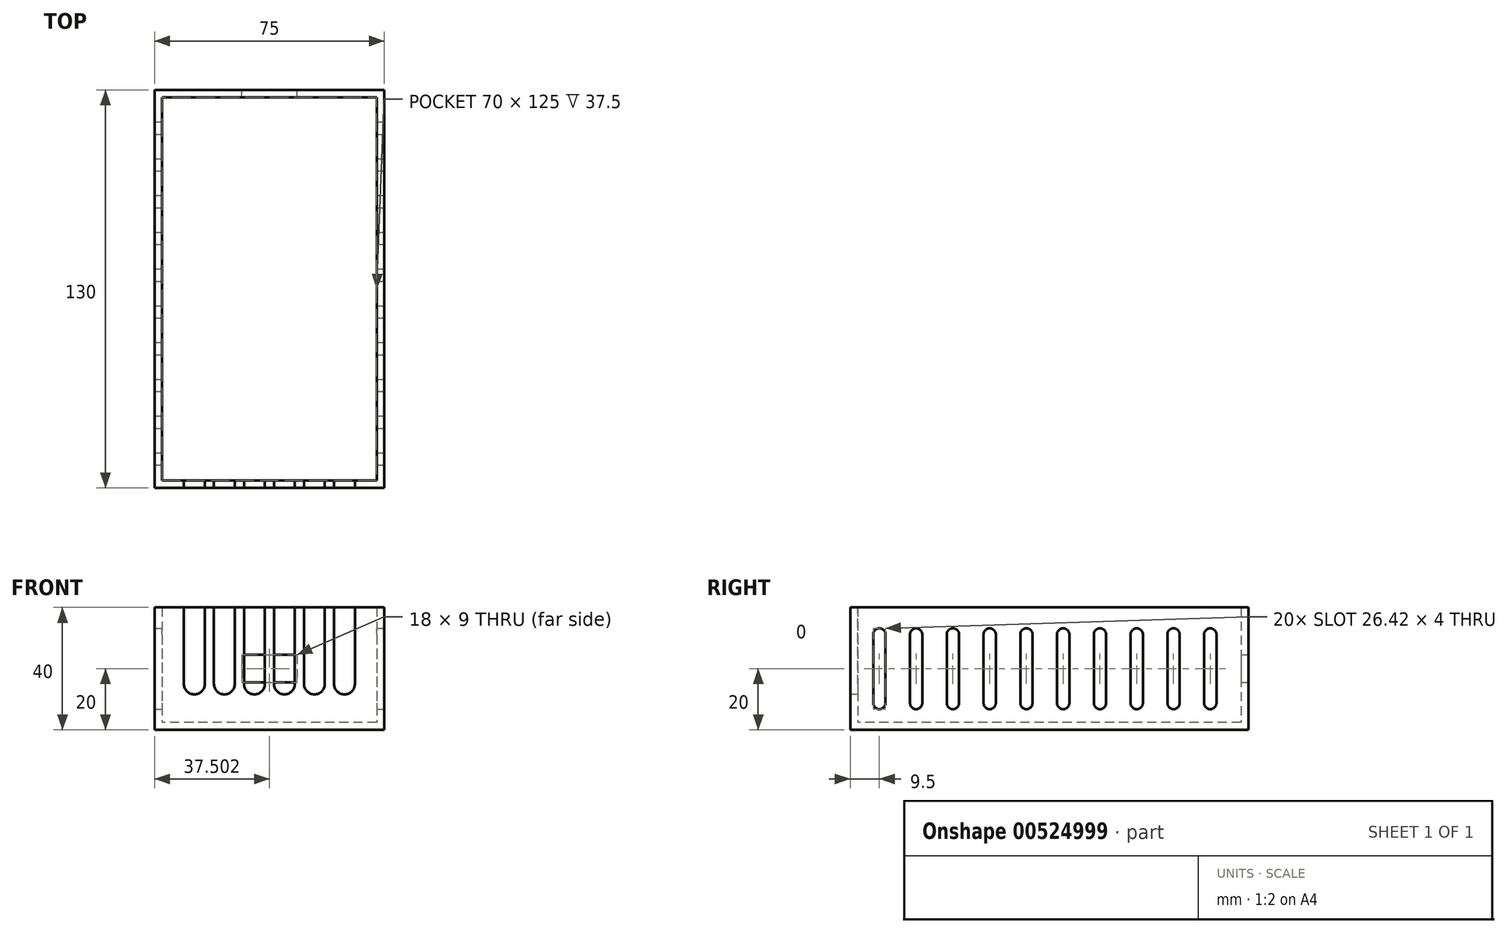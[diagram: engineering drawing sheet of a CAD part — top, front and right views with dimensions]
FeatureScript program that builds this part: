
annotation { "Feature Type Name" : "Feature", "Feature Type Description" : "" }
export const myFeature = defineFeature(function(context is Context, id is Id, definition is map)
    precondition{}
    {
        {
            var Q0;
            Q0=qCreatedBy(makeId("Top.planeOp"),FACE);
            var sketch = newSketch(context, id + "F0", { "sketchPlane" : qUnion([Q0])});
            skLineSegment(sketch, "E0.bottom", {"start": v(40.58, 65) * mm, "end": v(-34.42, 65) * mm});
            skLineSegment(sketch, "E0.top", {"start": v(40.58, -65) * mm, "end": v(-34.42, -65) * mm});
            skLineSegment(sketch, "E0.left", {"start": v(40.58, 65) * mm, "end": v(40.58, -65) * mm});
            skLineSegment(sketch, "E0.right", {"start": v(-34.42, 65) * mm, "end": v(-34.42, -65) * mm});
            skPoint(sketch, "E0.middle", {"position": v(3.08, 0) * mm});
            skSolve(sketch);
        }
        {
            var Q0;
            Q0=makeQuery(id+"F0.imprint","IMPRINT",FACE,{"disambiguationData":[TD([[makeQuery(id+"F0.imprint","IMPRINT",EDGE,{"derivedFrom":sQuery(id+"F0.wireOp",EDGE,"E0.bottom")}),1.0]])]});
            extrude(context, id + "F1", {"entities" : qUnion([Q0]), "depth" : 40 * mm, "offsetDistance" : 25 * mm});
        }
        {
            var Q0;
            Q0=makeQuery(id+"F1.opExtrude","CAP_FACE",FACE,{"disambiguationData":[OSD([sQuery(id+"F0.wireOp",EDGE,"E0.bottom"),sQuery(id+"F0.wireOp",EDGE,"E0.top"),sQuery(id+"F0.wireOp",EDGE,"E0.left"),sQuery(id+"F0.wireOp",EDGE,"E0.right")])],"isStart":false});
            shell(context, id + "F2", {"entities" : qUnion([Q0]), "thickness" : 2.5 * mm});
        }
        {
            var Q0;
            Q0=makeQuery(id+"F1.opExtrude","SWEPT_FACE",FACE,{"disambiguationData":[OSD([sQuery(id+"F0.wireOp",EDGE,"E0.top")])]});
            var sketch = newSketch(context, id + "F3", { "sketchPlane" : qUnion([Q0])});
            skLineSegment(sketch, "E1.bottom", {"start": v(-24.82, 40) * mm, "end": v(-18.02, 40) * mm});
            skLineSegment(sketch, "E1.left", {"start": v(-24.82, 40) * mm, "end": v(-24.82, 15) * mm});
            skLineSegment(sketch, "E1.right", {"start": v(-18.02, 40) * mm, "end": v(-18.02, 15) * mm});
            skArc(sketch, "E2", {"start": v(-24.82, 15) * mm, "mid": v(-21.42, 11.6) * mm, "end": v(-18.02, 15) * mm});
            skPoint(sketch, "E2.centerSnap0", {"position": v(-21.42, 20) * mm});
            skPoint(sketch, "E3.orphan", {"position": v(-18.02, 20) * mm});
            skPoint(sketch, "E4.orphan", {"position": v(-24.82, 20) * mm});
            skLineSegment(sketch, "E5.1.0.0", {"start": v(-15.02, 40) * mm, "end": v(-15.02, 15) * mm});
            skLineSegment(sketch, "E5.1.0.1", {"start": v(-15.02, 40) * mm, "end": v(-8.22, 40) * mm});
            skLineSegment(sketch, "E5.1.0.2", {"start": v(-8.22, 40) * mm, "end": v(-8.22, 15) * mm});
            skPoint(sketch, "E5.1.0.3", {"position": v(-15.02, 20) * mm});
            skPoint(sketch, "E5.1.0.4", {"position": v(-8.22, 20) * mm});
            skPoint(sketch, "E5.1.0.5", {"position": v(-11.62, 20) * mm});
            skArc(sketch, "E5.1.0.6", {"start": v(-15.02, 15) * mm, "mid": v(-11.62, 11.6) * mm, "end": v(-8.22, 15) * mm});
            skLineSegment(sketch, "E5.2.0.0", {"start": v(-5.22, 40) * mm, "end": v(-5.22, 15) * mm});
            skLineSegment(sketch, "E5.2.0.1", {"start": v(-5.22, 40) * mm, "end": v(1.58, 40) * mm});
            skLineSegment(sketch, "E5.2.0.2", {"start": v(1.58, 40) * mm, "end": v(1.58, 15) * mm});
            skPoint(sketch, "E5.2.0.3", {"position": v(-5.22, 20) * mm});
            skPoint(sketch, "E5.2.0.4", {"position": v(1.58, 20) * mm});
            skPoint(sketch, "E5.2.0.5", {"position": v(-1.82, 20) * mm});
            skArc(sketch, "E5.2.0.6", {"start": v(-5.22, 15) * mm, "mid": v(-1.82, 11.6) * mm, "end": v(1.58, 15) * mm});
            skLineSegment(sketch, "E5.3.0.0", {"start": v(4.58, 40) * mm, "end": v(4.58, 15) * mm});
            skLineSegment(sketch, "E5.3.0.1", {"start": v(4.58, 40) * mm, "end": v(11.38, 40) * mm});
            skLineSegment(sketch, "E5.3.0.2", {"start": v(11.38, 40) * mm, "end": v(11.38, 15) * mm});
            skPoint(sketch, "E5.3.0.3", {"position": v(4.58, 20) * mm});
            skPoint(sketch, "E5.3.0.4", {"position": v(11.38, 20) * mm});
            skPoint(sketch, "E5.3.0.5", {"position": v(7.98, 20) * mm});
            skArc(sketch, "E5.3.0.6", {"start": v(4.58, 15) * mm, "mid": v(7.98, 11.6) * mm, "end": v(11.38, 15) * mm});
            skLineSegment(sketch, "E5.4.0.0", {"start": v(14.38, 40) * mm, "end": v(14.38, 15) * mm});
            skLineSegment(sketch, "E5.4.0.1", {"start": v(14.38, 40) * mm, "end": v(21.18, 40) * mm});
            skLineSegment(sketch, "E5.4.0.2", {"start": v(21.18, 40) * mm, "end": v(21.18, 15) * mm});
            skPoint(sketch, "E5.4.0.3", {"position": v(14.38, 20) * mm});
            skPoint(sketch, "E5.4.0.4", {"position": v(21.18, 20) * mm});
            skPoint(sketch, "E5.4.0.5", {"position": v(17.78, 20) * mm});
            skArc(sketch, "E5.4.0.6", {"start": v(14.38, 15) * mm, "mid": v(17.78, 11.6) * mm, "end": v(21.18, 15) * mm});
            skLineSegment(sketch, "E5.5.0.0", {"start": v(24.18, 40) * mm, "end": v(24.18, 15) * mm});
            skLineSegment(sketch, "E5.5.0.1", {"start": v(24.18, 40) * mm, "end": v(30.98, 40) * mm});
            skLineSegment(sketch, "E5.5.0.2", {"start": v(30.98, 40) * mm, "end": v(30.98, 15) * mm});
            skPoint(sketch, "E5.5.0.3", {"position": v(24.18, 20) * mm});
            skPoint(sketch, "E5.5.0.4", {"position": v(30.98, 20) * mm});
            skPoint(sketch, "E5.5.0.5", {"position": v(27.58, 20) * mm});
            skArc(sketch, "E5.5.0.6", {"start": v(24.18, 15) * mm, "mid": v(27.58, 11.6) * mm, "end": v(30.98, 15) * mm});
            skLineSegment(sketch, "E5.direction1", {"start": v(-24.82, 15) * mm, "end": v(-15.02, 15) * mm, "construction": true});
            skSolve(sketch);
        }
        {
            var Q0;
            Q0=makeQuery(id+"F3.imprint","IMPRINT",FACE,{"disambiguationData":[TD([[makeQuery(id+"F3.imprint","IMPRINT",EDGE,{"derivedFrom":sQuery(id+"F3.wireOp",EDGE,"E1.bottom")}),1.0]])]});
            var Q1;
            Q1=makeQuery(id+"F3.imprint","IMPRINT",FACE,{"disambiguationData":[TD([[makeQuery(id+"F3.imprint","IMPRINT",EDGE,{"derivedFrom":sQuery(id+"F3.wireOp",EDGE,"E5.1.0.0")}),1.0]])]});
            var Q2;
            Q2=makeQuery(id+"F3.imprint","IMPRINT",FACE,{"disambiguationData":[TD([[makeQuery(id+"F3.imprint","IMPRINT",EDGE,{"derivedFrom":sQuery(id+"F3.wireOp",EDGE,"E5.2.0.0")}),1.0]])]});
            var Q3;
            Q3=makeQuery(id+"F3.imprint","IMPRINT",FACE,{"disambiguationData":[TD([[makeQuery(id+"F3.imprint","IMPRINT",EDGE,{"derivedFrom":sQuery(id+"F3.wireOp",EDGE,"E5.3.0.0")}),1.0]])]});
            var Q4;
            Q4=makeQuery(id+"F3.imprint","IMPRINT",FACE,{"disambiguationData":[TD([[makeQuery(id+"F3.imprint","IMPRINT",EDGE,{"derivedFrom":sQuery(id+"F3.wireOp",EDGE,"E5.4.0.0")}),1.0]])]});
            var Q5;
            Q5=makeQuery(id+"F3.imprint","IMPRINT",FACE,{"disambiguationData":[TD([[makeQuery(id+"F3.imprint","IMPRINT",EDGE,{"derivedFrom":sQuery(id+"F3.wireOp",EDGE,"E5.5.0.0")}),1.0]])]});
            var Q6;
            Q6=makeQuery(id+"F2.opShell","OFFSET_FACE",FACE,{"disambiguationData":[OSD([sQuery(id+"F0.wireOp",EDGE,"E0.top")])]});
            extrude(context, id + "F4", {"entities" : qUnion([Q0, Q1, Q2, Q3, Q4, Q5]), "operationType" : NewBodyOperationType.REMOVE, "endBound" : BoundingType.UP_TO_SURFACE, "oppositeDirection" : true, "depth" : 25 * mm, "endBoundEntityFace" : qUnion([Q6]), "offsetDistance" : 25 * mm});
        }
        {
            var Q0;
            Q0=makeQuery(id+"F1.opExtrude","SWEPT_FACE",FACE,{"disambiguationData":[OSD([sQuery(id+"F0.wireOp",EDGE,"E0.bottom")])]});
            var sketch = newSketch(context, id + "F5", { "sketchPlane" : qUnion([Q0])});
            skLineSegment(sketch, "E6", {"start": v(-3.08, 40) * mm, "end": v(-3.08, 0) * mm, "construction": true});
            skLineSegment(sketch, "E7", {"start": v(-40.58, 20) * mm, "end": v(34.42, 20) * mm, "construction": true});
            skLineSegment(sketch, "E8.bottom", {"start": v(5.92, 24.5) * mm, "end": v(-12.08, 24.5) * mm});
            skLineSegment(sketch, "E8.top", {"start": v(5.92, 15.5) * mm, "end": v(-12.08, 15.5) * mm});
            skLineSegment(sketch, "E8.left", {"start": v(5.92, 24.5) * mm, "end": v(5.92, 15.5) * mm});
            skLineSegment(sketch, "E8.right", {"start": v(-12.08, 24.5) * mm, "end": v(-12.08, 15.5) * mm});
            skPoint(sketch, "E8.middle", {"position": v(-3.08, 20) * mm});
            skSolve(sketch);
        }
        {
            var Q0;
            Q0=makeQuery(id+"F5.imprint","IMPRINT",FACE,{"disambiguationData":[TD([[makeQuery(id+"F5.imprint","IMPRINT",EDGE,{"derivedFrom":sQuery(id+"F5.wireOp",EDGE,"E8.bottom")}),1.0]])]});
            var Q1;
            Q1=makeQuery(id+"F2.opShell","OFFSET_FACE",FACE,{"disambiguationData":[OSD([sQuery(id+"F0.wireOp",EDGE,"E0.bottom")])]});
            extrude(context, id + "F6", {"entities" : qUnion([Q0]), "operationType" : NewBodyOperationType.REMOVE, "endBound" : BoundingType.UP_TO_SURFACE, "oppositeDirection" : true, "depth" : 25 * mm, "endBoundEntityFace" : qUnion([Q1]), "offsetDistance" : 25 * mm});
        }
        {
            var Q0;
            Q0=makeQuery(id+"F1.opExtrude","SWEPT_FACE",FACE,{"disambiguationData":[OSD([sQuery(id+"F0.wireOp",EDGE,"E0.left")])]});
            var sketch = newSketch(context, id + "F7", { "sketchPlane" : qUnion([Q0])});
            skLineSegment(sketch, "E9", {"start": v(0, 40) * mm, "end": v(0, 0) * mm, "construction": true});
            skLineSegment(sketch, "E10", {"start": v(-65, 20) * mm, "end": v(65, 20) * mm, "construction": true});
            skLineSegment(sketch, "E11.left", {"start": v(-53.5, 31.2) * mm, "end": v(-53.5, 8.8) * mm});
            skLineSegment(sketch, "E11.right", {"start": v(-57.5, 31.2) * mm, "end": v(-57.5, 8.8) * mm});
            skPoint(sketch, "E11.middle", {"position": v(-55.5, 20) * mm});
            skArc(sketch, "E12", {"start": v(-57.5, 8.8) * mm, "mid": v(-55.5, 6.8) * mm, "end": v(-53.5, 8.8) * mm});
            skPoint(sketch, "E12.centerSnap0", {"position": v(-55.5, 7.22) * mm});
            skArc(sketch, "E13", {"start": v(-53.5, 31.2) * mm, "mid": v(-55.5, 33.2) * mm, "end": v(-57.5, 31.2) * mm});
            skPoint(sketch, "E14.orphan", {"position": v(-53.5, 32.83) * mm});
            skPoint(sketch, "E15.orphan", {"position": v(-57.5, 32.73) * mm});
            skPoint(sketch, "E16.orphan", {"position": v(-53.5, 7.27) * mm});
            skPoint(sketch, "E17.orphan", {"position": v(-57.5, 7.17) * mm});
            skPoint(sketch, "E18.1.0.0", {"position": v(-45.5, 7.17) * mm});
            skPoint(sketch, "E18.1.0.1", {"position": v(-45.5, 32.73) * mm});
            skPoint(sketch, "E18.1.0.2", {"position": v(-41.5, 7.27) * mm});
            skPoint(sketch, "E18.1.0.3", {"position": v(-43.5, 20) * mm});
            skLineSegment(sketch, "E18.1.0.4", {"start": v(-41.5, 31.2) * mm, "end": v(-41.5, 8.8) * mm});
            skLineSegment(sketch, "E18.1.0.5", {"start": v(-45.5, 31.2) * mm, "end": v(-45.5, 8.8) * mm});
            skPoint(sketch, "E18.1.0.6", {"position": v(-41.5, 32.83) * mm});
            skPoint(sketch, "E18.1.0.7", {"position": v(-43.5, 7.22) * mm});
            skArc(sketch, "E18.1.0.8", {"start": v(-45.5, 8.8) * mm, "mid": v(-43.5, 6.8) * mm, "end": v(-41.5, 8.8) * mm});
            skArc(sketch, "E18.1.0.9", {"start": v(-41.5, 31.2) * mm, "mid": v(-43.5, 33.2) * mm, "end": v(-45.5, 31.2) * mm});
            skPoint(sketch, "E18.2.0.0", {"position": v(-33.5, 7.17) * mm});
            skPoint(sketch, "E18.2.0.1", {"position": v(-33.5, 32.73) * mm});
            skPoint(sketch, "E18.2.0.2", {"position": v(-29.5, 7.27) * mm});
            skPoint(sketch, "E18.2.0.3", {"position": v(-31.5, 20) * mm});
            skLineSegment(sketch, "E18.2.0.4", {"start": v(-29.5, 31.2) * mm, "end": v(-29.5, 8.8) * mm});
            skLineSegment(sketch, "E18.2.0.5", {"start": v(-33.5, 31.2) * mm, "end": v(-33.5, 8.8) * mm});
            skPoint(sketch, "E18.2.0.6", {"position": v(-29.5, 32.83) * mm});
            skPoint(sketch, "E18.2.0.7", {"position": v(-31.5, 7.22) * mm});
            skArc(sketch, "E18.2.0.8", {"start": v(-33.5, 8.8) * mm, "mid": v(-31.5, 6.8) * mm, "end": v(-29.5, 8.8) * mm});
            skArc(sketch, "E18.2.0.9", {"start": v(-29.5, 31.2) * mm, "mid": v(-31.5, 33.2) * mm, "end": v(-33.5, 31.2) * mm});
            skPoint(sketch, "E18.3.0.0", {"position": v(-21.5, 7.17) * mm});
            skPoint(sketch, "E18.3.0.1", {"position": v(-21.5, 32.73) * mm});
            skPoint(sketch, "E18.3.0.2", {"position": v(-17.5, 7.27) * mm});
            skPoint(sketch, "E18.3.0.3", {"position": v(-19.5, 20) * mm});
            skLineSegment(sketch, "E18.3.0.4", {"start": v(-17.5, 31.2) * mm, "end": v(-17.5, 8.8) * mm});
            skLineSegment(sketch, "E18.3.0.5", {"start": v(-21.5, 31.2) * mm, "end": v(-21.5, 8.8) * mm});
            skPoint(sketch, "E18.3.0.6", {"position": v(-17.5, 32.83) * mm});
            skPoint(sketch, "E18.3.0.7", {"position": v(-19.5, 7.22) * mm});
            skArc(sketch, "E18.3.0.8", {"start": v(-21.5, 8.8) * mm, "mid": v(-19.5, 6.8) * mm, "end": v(-17.5, 8.8) * mm});
            skArc(sketch, "E18.3.0.9", {"start": v(-17.5, 31.2) * mm, "mid": v(-19.5, 33.2) * mm, "end": v(-21.5, 31.2) * mm});
            skPoint(sketch, "E18.4.0.0", {"position": v(-9.5, 7.17) * mm});
            skPoint(sketch, "E18.4.0.1", {"position": v(-9.5, 32.73) * mm});
            skPoint(sketch, "E18.4.0.2", {"position": v(-5.5, 7.27) * mm});
            skPoint(sketch, "E18.4.0.3", {"position": v(-7.5, 20) * mm});
            skLineSegment(sketch, "E18.4.0.4", {"start": v(-5.5, 31.2) * mm, "end": v(-5.5, 8.8) * mm});
            skLineSegment(sketch, "E18.4.0.5", {"start": v(-9.5, 31.2) * mm, "end": v(-9.5, 8.8) * mm});
            skPoint(sketch, "E18.4.0.6", {"position": v(-5.5, 32.83) * mm});
            skPoint(sketch, "E18.4.0.7", {"position": v(-7.5, 7.22) * mm});
            skArc(sketch, "E18.4.0.8", {"start": v(-9.5, 8.8) * mm, "mid": v(-7.5, 6.8) * mm, "end": v(-5.5, 8.8) * mm});
            skArc(sketch, "E18.4.0.9", {"start": v(-5.5, 31.2) * mm, "mid": v(-7.5, 33.2) * mm, "end": v(-9.5, 31.2) * mm});
            skPoint(sketch, "E18.5.0.0", {"position": v(2.5, 7.17) * mm});
            skPoint(sketch, "E18.5.0.1", {"position": v(2.5, 32.73) * mm});
            skPoint(sketch, "E18.5.0.2", {"position": v(6.5, 7.27) * mm});
            skPoint(sketch, "E18.5.0.3", {"position": v(4.5, 20) * mm});
            skLineSegment(sketch, "E18.5.0.4", {"start": v(6.5, 31.2) * mm, "end": v(6.5, 8.8) * mm});
            skLineSegment(sketch, "E18.5.0.5", {"start": v(2.5, 31.2) * mm, "end": v(2.5, 8.8) * mm});
            skPoint(sketch, "E18.5.0.6", {"position": v(6.5, 32.83) * mm});
            skPoint(sketch, "E18.5.0.7", {"position": v(4.5, 7.22) * mm});
            skArc(sketch, "E18.5.0.8", {"start": v(2.5, 8.8) * mm, "mid": v(4.5, 6.8) * mm, "end": v(6.5, 8.8) * mm});
            skArc(sketch, "E18.5.0.9", {"start": v(6.5, 31.2) * mm, "mid": v(4.5, 33.2) * mm, "end": v(2.5, 31.2) * mm});
            skPoint(sketch, "E18.6.0.0", {"position": v(14.5, 7.17) * mm});
            skPoint(sketch, "E18.6.0.1", {"position": v(14.5, 32.73) * mm});
            skPoint(sketch, "E18.6.0.2", {"position": v(18.5, 7.27) * mm});
            skPoint(sketch, "E18.6.0.3", {"position": v(16.5, 20) * mm});
            skLineSegment(sketch, "E18.6.0.4", {"start": v(18.5, 31.2) * mm, "end": v(18.5, 8.8) * mm});
            skLineSegment(sketch, "E18.6.0.5", {"start": v(14.5, 31.2) * mm, "end": v(14.5, 8.8) * mm});
            skPoint(sketch, "E18.6.0.6", {"position": v(18.5, 32.83) * mm});
            skPoint(sketch, "E18.6.0.7", {"position": v(16.5, 7.22) * mm});
            skArc(sketch, "E18.6.0.8", {"start": v(14.5, 8.8) * mm, "mid": v(16.5, 6.8) * mm, "end": v(18.5, 8.8) * mm});
            skArc(sketch, "E18.6.0.9", {"start": v(18.5, 31.2) * mm, "mid": v(16.5, 33.2) * mm, "end": v(14.5, 31.2) * mm});
            skPoint(sketch, "E18.7.0.0", {"position": v(26.5, 7.17) * mm});
            skPoint(sketch, "E18.7.0.1", {"position": v(26.5, 32.73) * mm});
            skPoint(sketch, "E18.7.0.2", {"position": v(30.5, 7.27) * mm});
            skPoint(sketch, "E18.7.0.3", {"position": v(28.5, 20) * mm});
            skLineSegment(sketch, "E18.7.0.4", {"start": v(30.5, 31.2) * mm, "end": v(30.5, 8.8) * mm});
            skLineSegment(sketch, "E18.7.0.5", {"start": v(26.5, 31.2) * mm, "end": v(26.5, 8.8) * mm});
            skPoint(sketch, "E18.7.0.6", {"position": v(30.5, 32.83) * mm});
            skPoint(sketch, "E18.7.0.7", {"position": v(28.5, 7.22) * mm});
            skArc(sketch, "E18.7.0.8", {"start": v(26.5, 8.8) * mm, "mid": v(28.5, 6.8) * mm, "end": v(30.5, 8.8) * mm});
            skArc(sketch, "E18.7.0.9", {"start": v(30.5, 31.2) * mm, "mid": v(28.5, 33.2) * mm, "end": v(26.5, 31.2) * mm});
            skPoint(sketch, "E18.8.0.0", {"position": v(38.5, 7.17) * mm});
            skPoint(sketch, "E18.8.0.1", {"position": v(38.5, 32.73) * mm});
            skPoint(sketch, "E18.8.0.2", {"position": v(42.5, 7.27) * mm});
            skPoint(sketch, "E18.8.0.3", {"position": v(40.5, 20) * mm});
            skLineSegment(sketch, "E18.8.0.4", {"start": v(42.5, 31.2) * mm, "end": v(42.5, 8.8) * mm});
            skLineSegment(sketch, "E18.8.0.5", {"start": v(38.5, 31.2) * mm, "end": v(38.5, 8.8) * mm});
            skPoint(sketch, "E18.8.0.6", {"position": v(42.5, 32.83) * mm});
            skPoint(sketch, "E18.8.0.7", {"position": v(40.5, 7.22) * mm});
            skArc(sketch, "E18.8.0.8", {"start": v(38.5, 8.8) * mm, "mid": v(40.5, 6.8) * mm, "end": v(42.5, 8.8) * mm});
            skArc(sketch, "E18.8.0.9", {"start": v(42.5, 31.2) * mm, "mid": v(40.5, 33.2) * mm, "end": v(38.5, 31.2) * mm});
            skPoint(sketch, "E18.9.0.0", {"position": v(50.5, 7.17) * mm});
            skPoint(sketch, "E18.9.0.1", {"position": v(50.5, 32.73) * mm});
            skPoint(sketch, "E18.9.0.2", {"position": v(54.5, 7.27) * mm});
            skPoint(sketch, "E18.9.0.3", {"position": v(52.5, 20) * mm});
            skLineSegment(sketch, "E18.9.0.4", {"start": v(54.5, 31.2) * mm, "end": v(54.5, 8.8) * mm});
            skLineSegment(sketch, "E18.9.0.5", {"start": v(50.5, 31.2) * mm, "end": v(50.5, 8.8) * mm});
            skPoint(sketch, "E18.9.0.6", {"position": v(54.5, 32.83) * mm});
            skPoint(sketch, "E18.9.0.7", {"position": v(52.5, 7.22) * mm});
            skArc(sketch, "E18.9.0.8", {"start": v(50.5, 8.8) * mm, "mid": v(52.5, 6.8) * mm, "end": v(54.5, 8.8) * mm});
            skArc(sketch, "E18.9.0.9", {"start": v(54.5, 31.2) * mm, "mid": v(52.5, 33.2) * mm, "end": v(50.5, 31.2) * mm});
            skLineSegment(sketch, "E18.direction1", {"start": v(-57.5, 7.17) * mm, "end": v(-45.5, 7.17) * mm, "construction": true});
            skSolve(sketch);
        }
        {
            var Q0;
            Q0=makeQuery(id+"F7.imprint","IMPRINT",FACE,{"disambiguationData":[TD([[makeQuery(id+"F7.imprint","IMPRINT",EDGE,{"derivedFrom":sQuery(id+"F7.wireOp",EDGE,"E11.left")}),-1.0]])]});
            var Q1;
            Q1=makeQuery(id+"F7.imprint","IMPRINT",FACE,{"disambiguationData":[TD([[makeQuery(id+"F7.imprint","IMPRINT",EDGE,{"derivedFrom":sQuery(id+"F7.wireOp",EDGE,"E18.2.0.4")}),-1.0]])]});
            var Q2;
            Q2=makeQuery(id+"F7.imprint","IMPRINT",FACE,{"disambiguationData":[TD([[makeQuery(id+"F7.imprint","IMPRINT",EDGE,{"derivedFrom":sQuery(id+"F7.wireOp",EDGE,"E18.3.0.4")}),-1.0]])]});
            var Q3;
            Q3=makeQuery(id+"F7.imprint","IMPRINT",FACE,{"disambiguationData":[TD([[makeQuery(id+"F7.imprint","IMPRINT",EDGE,{"derivedFrom":sQuery(id+"F7.wireOp",EDGE,"E18.4.0.4")}),-1.0]])]});
            var Q4;
            Q4=makeQuery(id+"F7.imprint","IMPRINT",FACE,{"disambiguationData":[TD([[makeQuery(id+"F7.imprint","IMPRINT",EDGE,{"derivedFrom":sQuery(id+"F7.wireOp",EDGE,"E18.5.0.4")}),-1.0]])]});
            var Q5;
            Q5=makeQuery(id+"F7.imprint","IMPRINT",FACE,{"disambiguationData":[TD([[makeQuery(id+"F7.imprint","IMPRINT",EDGE,{"derivedFrom":sQuery(id+"F7.wireOp",EDGE,"E18.6.0.4")}),-1.0]])]});
            var Q6;
            Q6=makeQuery(id+"F7.imprint","IMPRINT",FACE,{"disambiguationData":[TD([[makeQuery(id+"F7.imprint","IMPRINT",EDGE,{"derivedFrom":sQuery(id+"F7.wireOp",EDGE,"E18.7.0.4")}),-1.0]])]});
            var Q7;
            Q7=makeQuery(id+"F7.imprint","IMPRINT",FACE,{"disambiguationData":[TD([[makeQuery(id+"F7.imprint","IMPRINT",EDGE,{"derivedFrom":sQuery(id+"F7.wireOp",EDGE,"E18.8.0.4")}),-1.0]])]});
            var Q8;
            Q8=makeQuery(id+"F7.imprint","IMPRINT",FACE,{"disambiguationData":[TD([[makeQuery(id+"F7.imprint","IMPRINT",EDGE,{"derivedFrom":sQuery(id+"F7.wireOp",EDGE,"E18.9.0.4")}),-1.0]])]});
            var Q9;
            Q9=makeQuery(id+"F7.imprint","IMPRINT",FACE,{"disambiguationData":[TD([[makeQuery(id+"F7.imprint","IMPRINT",EDGE,{"derivedFrom":sQuery(id+"F7.wireOp",EDGE,"E18.1.0.4")}),-1.0]])]});
            var Q10;
            Q10=makeQuery(id+"F1.opExtrude","SWEPT_FACE",FACE,{"disambiguationData":[OSD([sQuery(id+"F0.wireOp",EDGE,"E0.right")])]});
            extrude(context, id + "F8", {"entities" : qUnion([Q0, Q1, Q2, Q3, Q4, Q5, Q6, Q7, Q8, Q9]), "operationType" : NewBodyOperationType.REMOVE, "endBound" : BoundingType.UP_TO_SURFACE, "oppositeDirection" : true, "depth" : 25 * mm, "endBoundEntityFace" : qUnion([Q10]), "offsetDistance" : 25 * mm});
        }
    });
